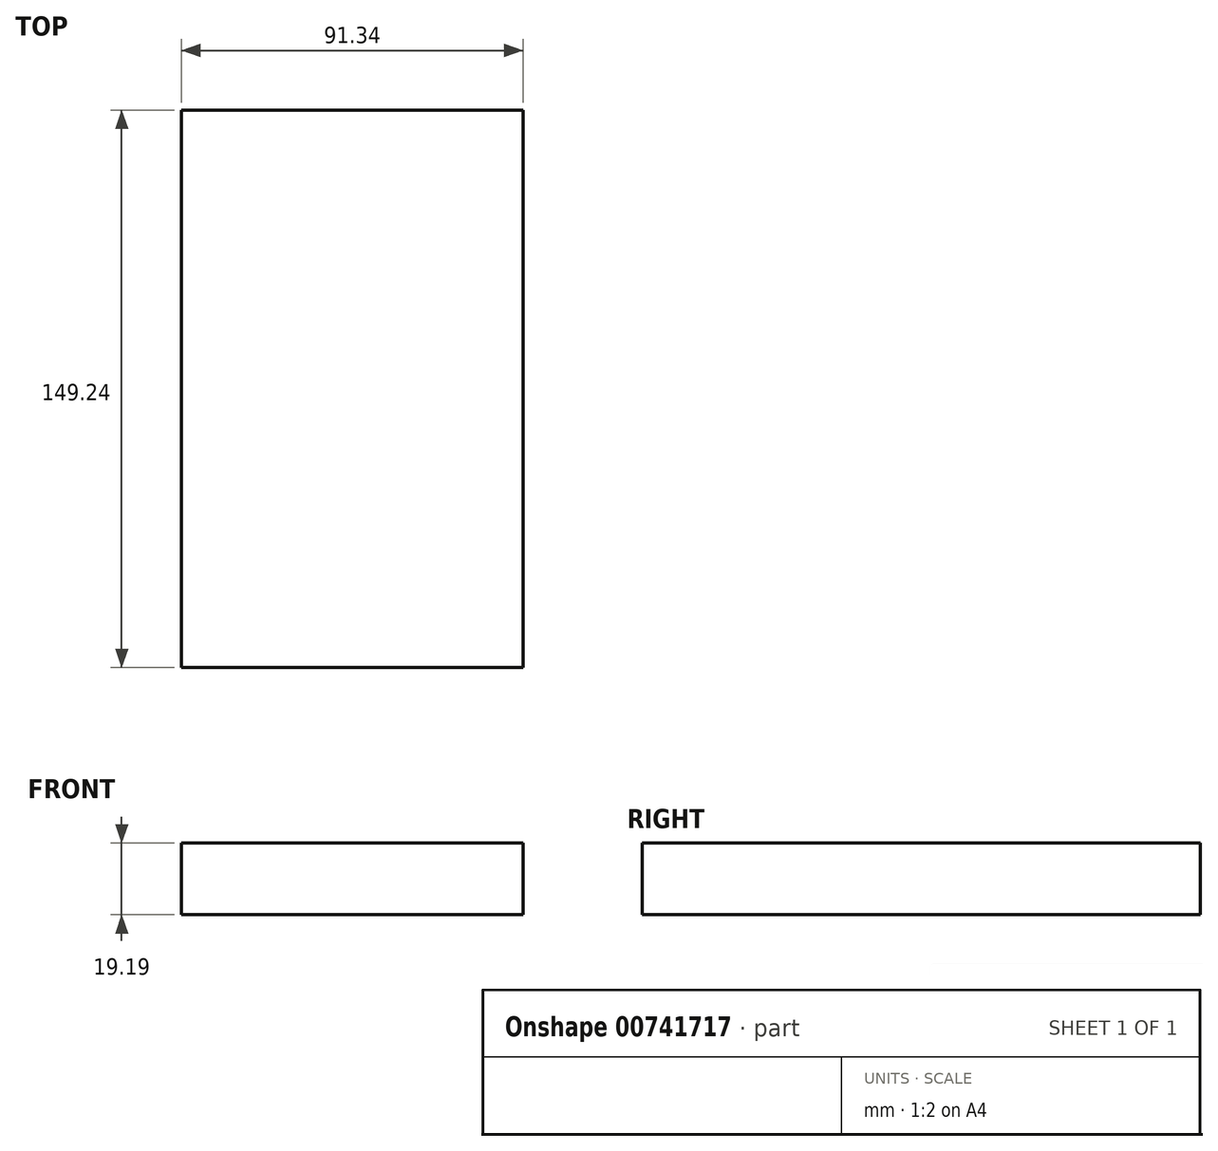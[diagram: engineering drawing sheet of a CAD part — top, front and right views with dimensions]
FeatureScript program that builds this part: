
annotation { "Feature Type Name" : "Feature", "Feature Type Description" : "" }
export const myFeature = defineFeature(function(context is Context, id is Id, definition is map)
    precondition{}
    {
        {
            var Q0;
            Q0=qCreatedBy(makeId("Top.planeOp"),FACE);
            var sketch = newSketch(context, id + "F0", { "sketchPlane" : qUnion([Q0])});
            skLineSegment(sketch, "E0.bottom", {"start": v(28.83, 23.47) * mm, "end": v(-62.5, 23.47) * mm});
            skLineSegment(sketch, "E0.top", {"start": v(28.83, 172.7) * mm, "end": v(-62.5, 172.7) * mm});
            skLineSegment(sketch, "E0.left", {"start": v(28.83, 23.47) * mm, "end": v(28.83, 172.7) * mm});
            skLineSegment(sketch, "E0.right", {"start": v(-62.5, 23.47) * mm, "end": v(-62.5, 172.7) * mm});
            skPoint(sketch, "E0.middle", {"position": v(-16.84, 98.09) * mm});
            skSolve(sketch);
        }
        {
            var Q0;
            Q0 = qSketchRegion(id + "F0", true);
            extrude(context, id + "F1", {"entities" : qUnion([Q0]), "depth" : 19.2 * mm, "offsetDistance" : 25.4 * mm});
        }
    });
